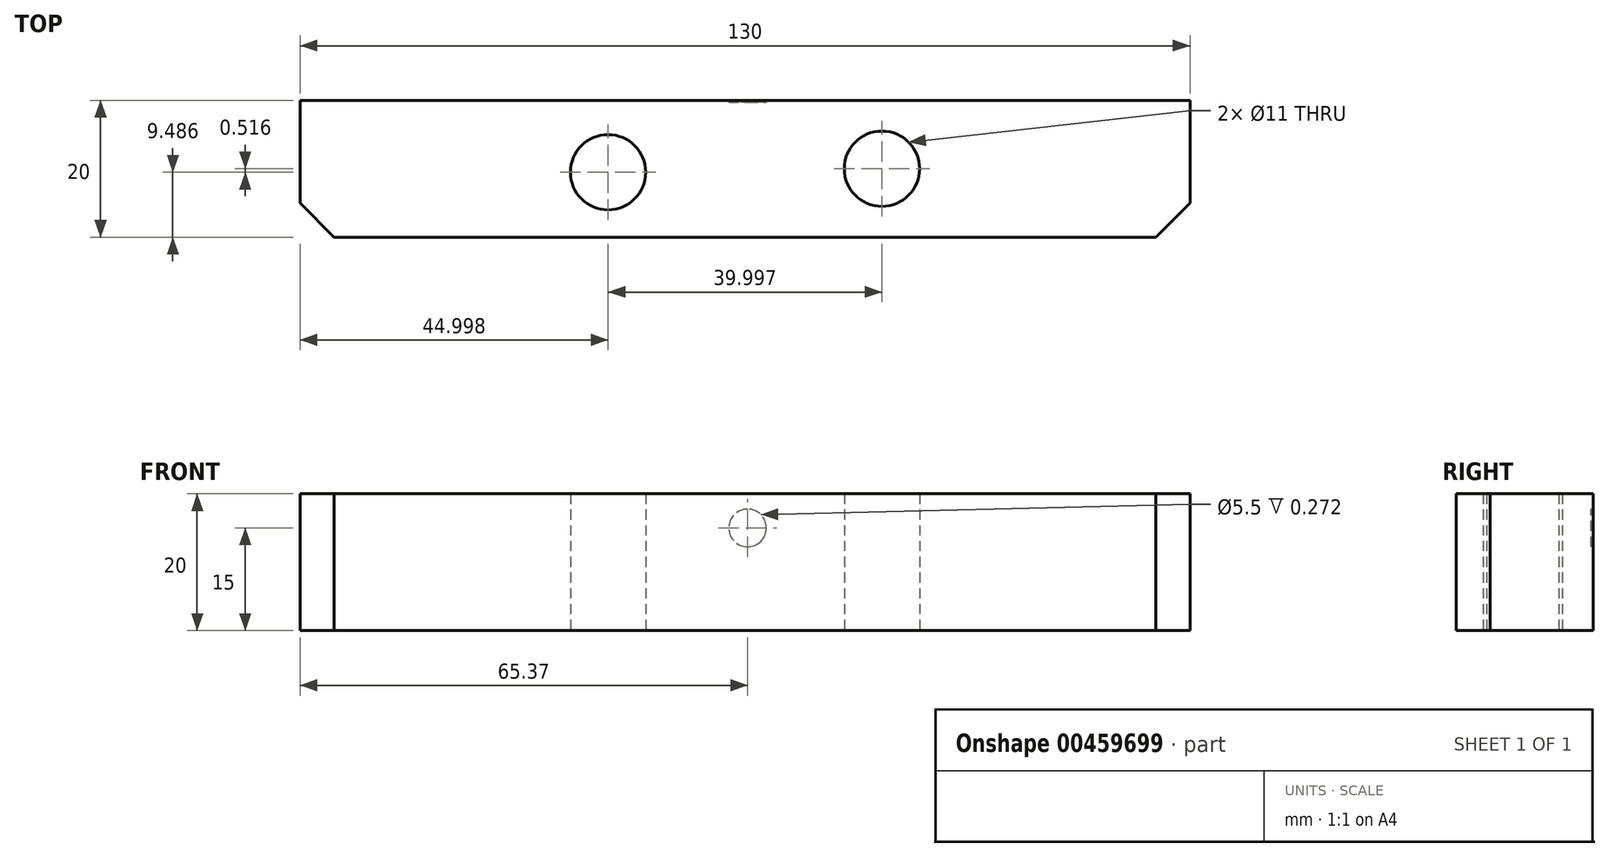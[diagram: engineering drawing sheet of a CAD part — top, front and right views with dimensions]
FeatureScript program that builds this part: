
annotation { "Feature Type Name" : "Feature", "Feature Type Description" : "" }
export const myFeature = defineFeature(function(context is Context, id is Id, definition is map)
    precondition{}
    {
        {
            var Q0;
            Q0=qCreatedBy(makeId("Top.planeOp"),FACE);
            var sketch = newSketch(context, id + "F0", { "sketchPlane" : qUnion([Q0])});
            skLineSegment(sketch, "E0", {"start": v(-65.37, 0.27) * mm, "end": v(64.63, 0.27) * mm});
            skLineSegment(sketch, "E1", {"start": v(64.63, 0.27) * mm, "end": v(64.63, -14.73) * mm});
            skLineSegment(sketch, "E2", {"start": v(-65.37, 0.27) * mm, "end": v(-65.37, -14.73) * mm});
            skLineSegment(sketch, "E3", {"start": v(-60.37, -19.73) * mm, "end": v(59.63, -19.73) * mm});
            skLineSegment(sketch, "E4", {"start": v(59.63, -19.73) * mm, "end": v(64.63, -14.73) * mm});
            skLineSegment(sketch, "E5", {"start": v(-60.37, -19.73) * mm, "end": v(-65.37, -14.73) * mm});
            skCircle(sketch, "E6", {"center": v(19.62, -9.73) * mm, "radius": 3.25 * mm});
            skCircle(sketch, "E7", {"center": v(19.62, -9.73) * mm, "radius": 5.5 * mm});
            skCircle(sketch, "E8", {"center": v(-20.37, -10.24) * mm, "radius": 3.25 * mm});
            skCircle(sketch, "E9", {"center": v(-20.37, -10.24) * mm, "radius": 5.5 * mm});
            skLineSegment(sketch, "E10.bottom", {"start": v(-60.41, 0.27) * mm, "end": v(-54.57, 0.27) * mm, "construction": true});
            skLineSegment(sketch, "E10.top", {"start": v(-60.41, -13.47) * mm, "end": v(-54.57, -13.47) * mm, "construction": true});
            skLineSegment(sketch, "E10.left", {"start": v(-60.41, 0.27) * mm, "end": v(-60.41, -13.47) * mm, "construction": true});
            skLineSegment(sketch, "E10.right", {"start": v(-54.57, 0.27) * mm, "end": v(-54.57, -13.47) * mm, "construction": true});
            skLineSegment(sketch, "E11.bottom", {"start": v(-3.61, 0.27) * mm, "end": v(3.8, 0.27) * mm, "construction": true});
            skLineSegment(sketch, "E11.top", {"start": v(-3.61, -13.7) * mm, "end": v(3.8, -13.7) * mm, "construction": true});
            skLineSegment(sketch, "E11.left", {"start": v(-3.61, 0.27) * mm, "end": v(-3.61, -13.7) * mm, "construction": true});
            skLineSegment(sketch, "E11.right", {"start": v(3.8, 0.27) * mm, "end": v(3.8, -13.7) * mm, "construction": true});
            skLineSegment(sketch, "E12.bottom", {"start": v(51.83, 0.27) * mm, "end": v(59.24, 0.27) * mm, "construction": true});
            skLineSegment(sketch, "E12.top", {"start": v(51.83, -13.7) * mm, "end": v(59.24, -13.7) * mm, "construction": true});
            skLineSegment(sketch, "E12.left", {"start": v(51.83, 0.27) * mm, "end": v(51.83, -13.7) * mm, "construction": true});
            skLineSegment(sketch, "E12.right", {"start": v(59.24, 0.27) * mm, "end": v(59.24, -13.7) * mm, "construction": true});
            skSolve(sketch);
        }
        {
            var Q0;
            Q0=qCreatedBy(makeId("Front.planeOp"),FACE);
            var sketch = newSketch(context, id + "F1", { "sketchPlane" : qUnion([Q0])});
            skLineSegment(sketch, "E13", {"start": v(65, 0) * mm, "end": v(65, 20) * mm});
            skLineSegment(sketch, "E14", {"start": v(65, 20) * mm, "end": v(-65, 20) * mm});
            skLineSegment(sketch, "E15", {"start": v(-65, 20) * mm, "end": v(-65, 0) * mm});
            skLineSegment(sketch, "E16", {"start": v(65, 0) * mm, "end": v(-65, 0) * mm});
            skCircle(sketch, "E17", {"center": v(-55, 15) * mm, "radius": 2.5 * mm});
            skCircle(sketch, "E18", {"center": v(0, 15) * mm, "radius": 2.5 * mm});
            skCircle(sketch, "E19", {"center": v(55, 15) * mm, "radius": 2.5 * mm});
            skLineSegment(sketch, "E20", {"start": v(-59.38, 20) * mm, "end": v(-59.38, 0) * mm, "construction": true});
            skLineSegment(sketch, "E21", {"start": v(59.38, 20) * mm, "end": v(59.38, 0) * mm, "construction": true});
            skSolve(sketch);
        }
        {
            var Q0;
            Q0=makeQuery(id+"F0.imprint","IMPRINT",FACE,{"disambiguationData":[TD([[makeQuery(id+"F0.imprint","IMPRINT",EDGE,{"derivedFrom":sQuery(id+"F0.wireOp",EDGE,"E0")}),-1.0]])]});
            extrude(context, id + "F2", {"entities" : qUnion([Q0]), "depth" : 20 * mm});
        }
        {
            var Q0;
            Q0=sQuery(id+"F0.wireOp",EDGE,"E9");
            extrude(context, id + "F3", {"bodyType" : ToolBodyType.SURFACE, "surfaceEntities" : qUnion([Q0]), "depth" : 5.5 * mm});
        }
        {
            var Q0;
            Q0=sQuery(id+"F1.wireOp",VERTEX,"E18.center");
            var Q1;
            Q1=makeQuery(id+"F2.opExtrude","SWEPT_BODY",BODY,{"disambiguationData":[OSD([sQuery(id+"F0.wireOp",EDGE,"E0"),sQuery(id+"F0.wireOp",EDGE,"E1"),sQuery(id+"F0.wireOp",EDGE,"E2"),sQuery(id+"F0.wireOp",EDGE,"E3"),sQuery(id+"F0.wireOp",EDGE,"E4"),sQuery(id+"F0.wireOp",EDGE,"E5"),sQuery(id+"F0.wireOp",EDGE,"E7"),sQuery(id+"F0.wireOp",EDGE,"E9")])]});
            hole(context, id + "F4", {"style" : HoleStyle.SIMPLE, "endStyle" : HoleEndStyle.BLIND, "holeDiameter" : 5.5 * mm, "holeDepth" : 12 * mm, "isTappedThrough" : true, "tappedDepth" : 12 * mm, "tapClearance" : 3, "locations" : qUnion([Q0]), "scope" : qUnion([Q1])});
        }
    });
